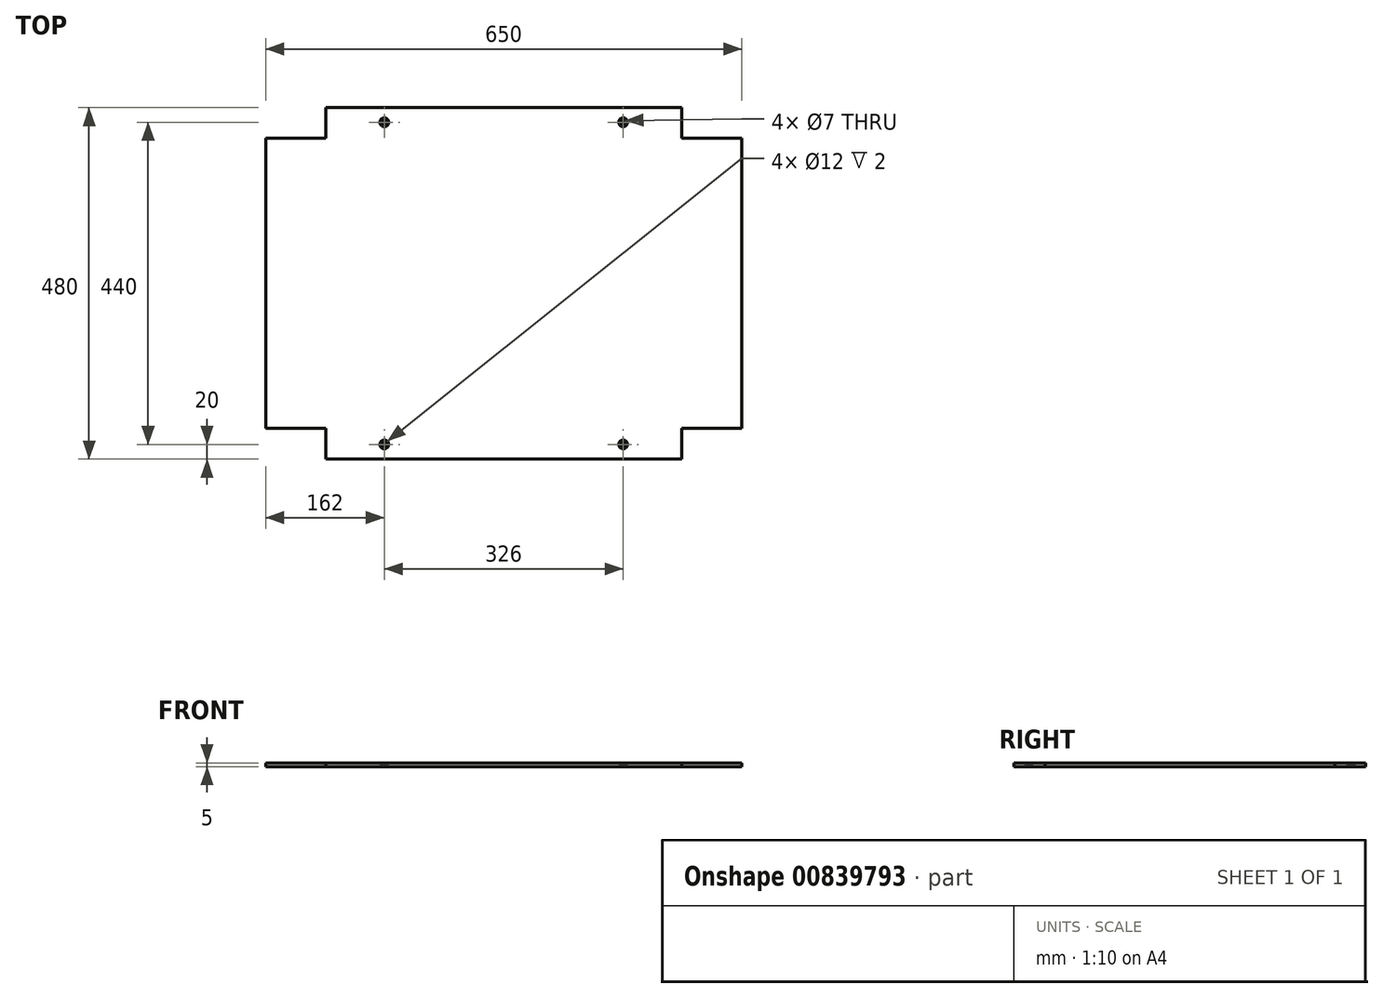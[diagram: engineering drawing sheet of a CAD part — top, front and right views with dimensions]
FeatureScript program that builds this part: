
annotation { "Feature Type Name" : "Feature", "Feature Type Description" : "" }
export const myFeature = defineFeature(function(context is Context, id is Id, definition is map)
    precondition{}
    {
        {
            var Q0;
            Q0=qCreatedBy(makeId("Top.planeOp"),FACE);
            var sketch = newSketch(context, id + "F0", { "sketchPlane" : qUnion([Q0])});
            skLineSegment(sketch, "E0.bottom", {"start": v(-325, 240) * mm, "end": v(325, 240) * mm});
            skLineSegment(sketch, "E0.top", {"start": v(-325, -240) * mm, "end": v(325, -240) * mm});
            skLineSegment(sketch, "E0.left", {"start": v(-325, 240) * mm, "end": v(-325, -240) * mm});
            skLineSegment(sketch, "E0.right", {"start": v(325, 240) * mm, "end": v(325, -240) * mm});
            skPoint(sketch, "E0.middle", {"position": v(0, 0) * mm});
            skLineSegment(sketch, "E1.bottom", {"start": v(-325, 240) * mm, "end": v(-243, 240) * mm});
            skLineSegment(sketch, "E1.top", {"start": v(-325, 198) * mm, "end": v(-243, 198) * mm});
            skLineSegment(sketch, "E1.left", {"start": v(-325, 240) * mm, "end": v(-325, 198) * mm});
            skLineSegment(sketch, "E1.right", {"start": v(-243, 240) * mm, "end": v(-243, 198) * mm});
            skLineSegment(sketch, "E2.MirrorCS", {"start": v(325, 198) * mm, "end": v(243, 198) * mm});
            skLineSegment(sketch, "E3.MirrorCS", {"start": v(243, 240) * mm, "end": v(243, 198) * mm});
            skLineSegment(sketch, "E4.MirrorCS", {"start": v(-325, -198) * mm, "end": v(-243, -198) * mm});
            skLineSegment(sketch, "E5.MirrorCS", {"start": v(-243, -240) * mm, "end": v(-243, -198) * mm});
            skLineSegment(sketch, "E6.MirrorCS", {"start": v(243, -240) * mm, "end": v(243, -198) * mm});
            skLineSegment(sketch, "E7.MirrorCS", {"start": v(325, -198) * mm, "end": v(243, -198) * mm});
            skSolve(sketch);
        }
        {
            var Q0;
            {var subQ3=sQuery(id+"F0.wireOp",EDGE,"E1.top");Q0=makeQuery(id+"F0.imprint","IMPRINT",FACE,{"disambiguationData":[TD([[makeQuery(id+"F0.imprint","IMPRINT",EDGE,{"derivedFrom":subQ3}),-1.0]])]});}
            extrude(context, id + "F1", {"entities" : qUnion([Q0]), "depth" : 5 * mm, "offsetDistance" : 25 * mm});
        }
        {
            var Q0;
            Q0=makeQuery(id+"F1.opExtrude","CAP_FACE",FACE,{"disambiguationData":[OSD([sQuery(id+"F0.wireOp",EDGE,"E0.bottom"),sQuery(id+"F0.wireOp",EDGE,"E0.top"),sQuery(id+"F0.wireOp",EDGE,"E0.left"),sQuery(id+"F0.wireOp",EDGE,"E0.right"),sQuery(id+"F0.wireOp",EDGE,"E1.top"),sQuery(id+"F0.wireOp",EDGE,"E1.right"),sQuery(id+"F0.wireOp",EDGE,"E2.MirrorCS"),sQuery(id+"F0.wireOp",EDGE,"E3.MirrorCS"),sQuery(id+"F0.wireOp",EDGE,"E4.MirrorCS"),sQuery(id+"F0.wireOp",EDGE,"E5.MirrorCS"),sQuery(id+"F0.wireOp",EDGE,"E6.MirrorCS"),sQuery(id+"F0.wireOp",EDGE,"E7.MirrorCS")])],"isStart":false});
            var sketch = newSketch(context, id + "F2", { "sketchPlane" : qUnion([Q0])});
            skPoint(sketch, "E8", {"position": v(-163, -220) * mm});
            skPoint(sketch, "E9.MirrorP", {"position": v(163, -220) * mm});
            skPoint(sketch, "E10.MirrorP", {"position": v(-163, 220) * mm});
            skPoint(sketch, "E11.MirrorP", {"position": v(163, 220) * mm});
            skSolve(sketch);
        }
        {
            var Q0;
            Q0=sQuery(id+"F2.wireOp",VERTEX,"E10.MirrorP");
            var Q1;
            Q1=sQuery(id+"F2.wireOp",VERTEX,"E8");
            var Q2;
            Q2=sQuery(id+"F2.wireOp",VERTEX,"E9.MirrorP");
            var Q3;
            Q3=sQuery(id+"F2.wireOp",VERTEX,"E11.MirrorP");
            var Q4;
            Q4=makeQuery(id+"F1.opExtrude","SWEPT_BODY",BODY,{"disambiguationData":[OSD([sQuery(id+"F0.wireOp",EDGE,"E0.bottom"),sQuery(id+"F0.wireOp",EDGE,"E0.top"),sQuery(id+"F0.wireOp",EDGE,"E0.left"),sQuery(id+"F0.wireOp",EDGE,"E0.right"),sQuery(id+"F0.wireOp",EDGE,"E1.top"),sQuery(id+"F0.wireOp",EDGE,"E1.right"),sQuery(id+"F0.wireOp",EDGE,"E2.MirrorCS"),sQuery(id+"F0.wireOp",EDGE,"E3.MirrorCS"),sQuery(id+"F0.wireOp",EDGE,"E4.MirrorCS"),sQuery(id+"F0.wireOp",EDGE,"E5.MirrorCS"),sQuery(id+"F0.wireOp",EDGE,"E6.MirrorCS"),sQuery(id+"F0.wireOp",EDGE,"E7.MirrorCS")])]});
            hole(context, id + "F3", {"style" : HoleStyle.C_BORE, "endStyle" : HoleEndStyle.THROUGH, "holeDiameter" : 7 * mm, "cBoreDiameter" : 12 * mm, "cBoreDepth" : 2 * mm, "majorDiameter" : 5 * mm, "isTappedThrough" : true, "tappedDepth" : 12 * mm, "tapClearance" : 3, "locations" : qUnion([Q0, Q1, Q2, Q3]), "scope" : qUnion([Q4])});
        }
    });
